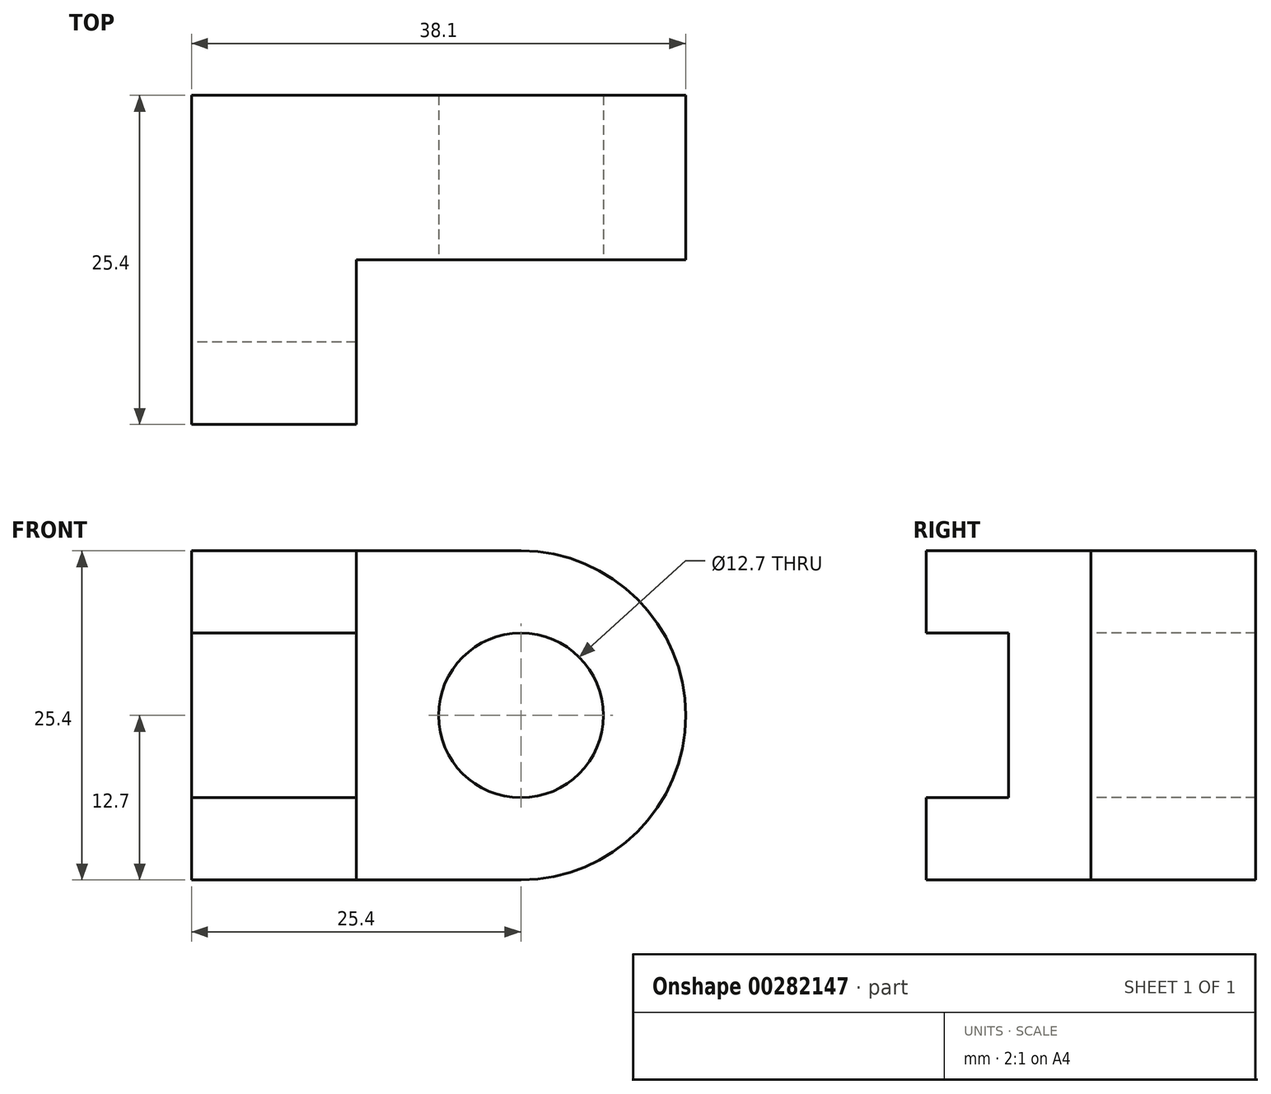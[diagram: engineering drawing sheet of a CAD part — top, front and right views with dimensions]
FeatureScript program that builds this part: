
annotation { "Feature Type Name" : "Feature", "Feature Type Description" : "" }
export const myFeature = defineFeature(function(context is Context, id is Id, definition is map)
    precondition{}
    {
        {
            var Q0;
            Q0=qCreatedBy(makeId("Front.planeOp"),FACE);
            var sketch = newSketch(context, id + "F0", { "sketchPlane" : qUnion([Q0])});
            skLineSegment(sketch, "E0", {"start": v(0, 0) * mm, "end": v(0, 25.4) * mm});
            skLineSegment(sketch, "E1", {"start": v(0, 25.4) * mm, "end": v(25.4, 25.4) * mm});
            skLineSegment(sketch, "E2", {"start": v(0, 0) * mm, "end": v(25.4, 0) * mm});
            skArc(sketch, "E3", {"start": v(25.4, 25.4) * mm, "mid": v(38.1, 12.7) * mm, "end": v(25.4, 0) * mm});
            skCircle(sketch, "E4", {"center": v(25.4, 12.7) * mm, "radius": 6.35 * mm});
            skSolve(sketch);
        }
        {
            var Q0;
            Q0=makeQuery(id+"F0.imprint","IMPRINT",FACE,{"disambiguationData":[TD([[makeQuery(id+"F0.imprint","IMPRINT",EDGE,{"derivedFrom":sQuery(id+"F0.wireOp",EDGE,"E0")}),-1.0]])]});
            extrude(context, id + "F1", {"entities" : qUnion([Q0]), "oppositeDirection" : true, "depth" : 12.7 * mm});
        }
        {
            var Q0;
            Q0=qCreatedBy(makeId("Right.planeOp"),FACE);
            var sketch = newSketch(context, id + "F2", { "sketchPlane" : qUnion([Q0])});
            skLineSegment(sketch, "E5", {"start": v(0, 25.4) * mm, "end": v(0, 0) * mm});
            skLineSegment(sketch, "E6", {"start": v(0, 0) * mm, "end": v(-12.7, 0) * mm});
            skLineSegment(sketch, "E7", {"start": v(-12.7, 0) * mm, "end": v(-12.7, 6.35) * mm});
            skLineSegment(sketch, "E8", {"start": v(-12.7, 6.35) * mm, "end": v(-6.35, 6.35) * mm});
            skLineSegment(sketch, "E9", {"start": v(-6.35, 6.35) * mm, "end": v(-6.35, 19.05) * mm});
            skLineSegment(sketch, "E10", {"start": v(-6.35, 19.05) * mm, "end": v(-12.7, 19.05) * mm});
            skLineSegment(sketch, "E11", {"start": v(-12.7, 19.05) * mm, "end": v(-12.7, 25.4) * mm});
            skLineSegment(sketch, "E12", {"start": v(-12.7, 25.4) * mm, "end": v(0, 25.4) * mm});
            skSolve(sketch);
        }
        {
            var Q0;
            Q0=makeQuery(id+"F2.imprint","IMPRINT",FACE,{"disambiguationData":[TD([[makeQuery(id+"F2.imprint","IMPRINT",EDGE,{"derivedFrom":sQuery(id+"F2.wireOp",EDGE,"E5")}),-1.0]])]});
            extrude(context, id + "F3", {"entities" : qUnion([Q0]), "operationType" : NewBodyOperationType.ADD, "depth" : 12.7 * mm});
        }
    });
